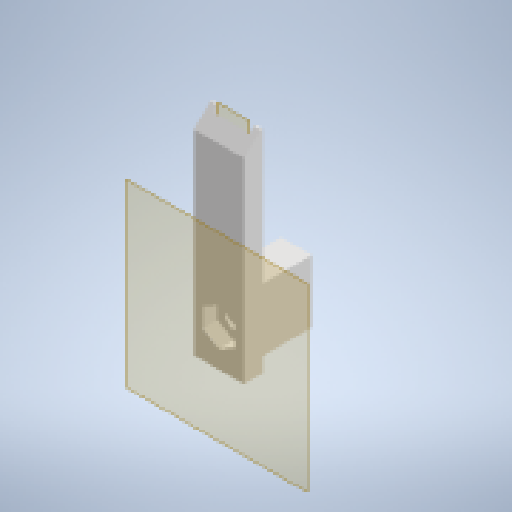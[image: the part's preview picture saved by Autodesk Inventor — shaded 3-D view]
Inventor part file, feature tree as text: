
AUTODESK INVENTOR PART (.ipt)
format: ipt  version: 2023.3 (Build 273359000, 359)  size: 245,248 bytes
history: native  units: in
note: dims shown in document units (in); Inventor stores cm internally (conversion verified against a paired STEP export)
features: reference x12, extrude x7, sketch x7, other x5, plane x2, chamfer x1, projected_geometry x1
ambient origin geometry x8: Origin, YZ Plane, XZ Plane, XY Plane, X Axis, Y Axis, Z Axis, Center Point
bodies: Body1 (feature_tree)
feature tree (35):
  plane  "Work Plane3"
  extrude  "side"  Depth=0.0591in
  extrude  "side_tabs"  Depth=0.0079in
  extrude  "fill_gaps"  Depth=0.0295in TaperAngle=0.0deg
  extrude  "fill_gaps_2"  Depth=0.3858in TaperAngle=0.0deg
  chamfer  "Chamfer1"  Distance=0.0787in Angle=45.0deg
  extrude  "sliding_block"  Depth=0.0069in
  plane  "Work Plane4"
  extrude  "screw_hole"  Depth=0.0069in
  extrude  "nut_slot"  TaperAngle=0.0deg  [1 undecoded]
  sketch  "Sketch8"  dims[d40=0.0591in d41=0.0in d71=0.0394in]
  reference  "Reference43"
  reference  "Reference44"
  reference  "Reference45"
  reference  "Reference46"
  sketch  "Sketch14"  dims[d72=0.0394in d73=0.0079in]
  reference  "Reference47"
  reference  "Reference48"
  sketch  "Sketch15"  dims[d74=0.0079in d75=0.0295in d76=0.0in]
  projected_geometry  "Projected Loop2"
  sketch  "Sketch16"  dims[d79=0.5709in d80=0.0in d81=0.3858in d82=0.0in d83=0.0787in d84=0.0787in d85=45.0deg]
  sketch  "Sketch17"  dims[d86=0.0069in d87=0.0069in]
  reference  "Reference51"
  reference  "Reference52"
  reference  "Reference53"
  reference  "Reference54"
  sketch  "Sketch19"  dims[d88=0.0069in d89=0.0069in]
  reference  "Reference56"
  sketch  "Sketch20"  dims[d90=0.2835in d91=0.0in d95=0.0in d96=0.0in d99=0.02in d100=0.0079in d102=0.1575in d103=0.0709in d104=0.0in]
  reference  "Reference60"
  parser-record x2  (decoder bookkeeping rows leaked as tree rows — omitted from the tree; the rows remain in map.json)
  other  "full_assembly.iam"
  other  "probe_holder:1"
  other  "surgical_holder:1"
note: 1 required parameter value undecoded (feature->parameter linkage not recoverable at this tier; creation-order binding heuristic only, values carry confidence <= 0.55)
note: 2 file-system paths scrubbed to <path> (originals preserved in map.json)
